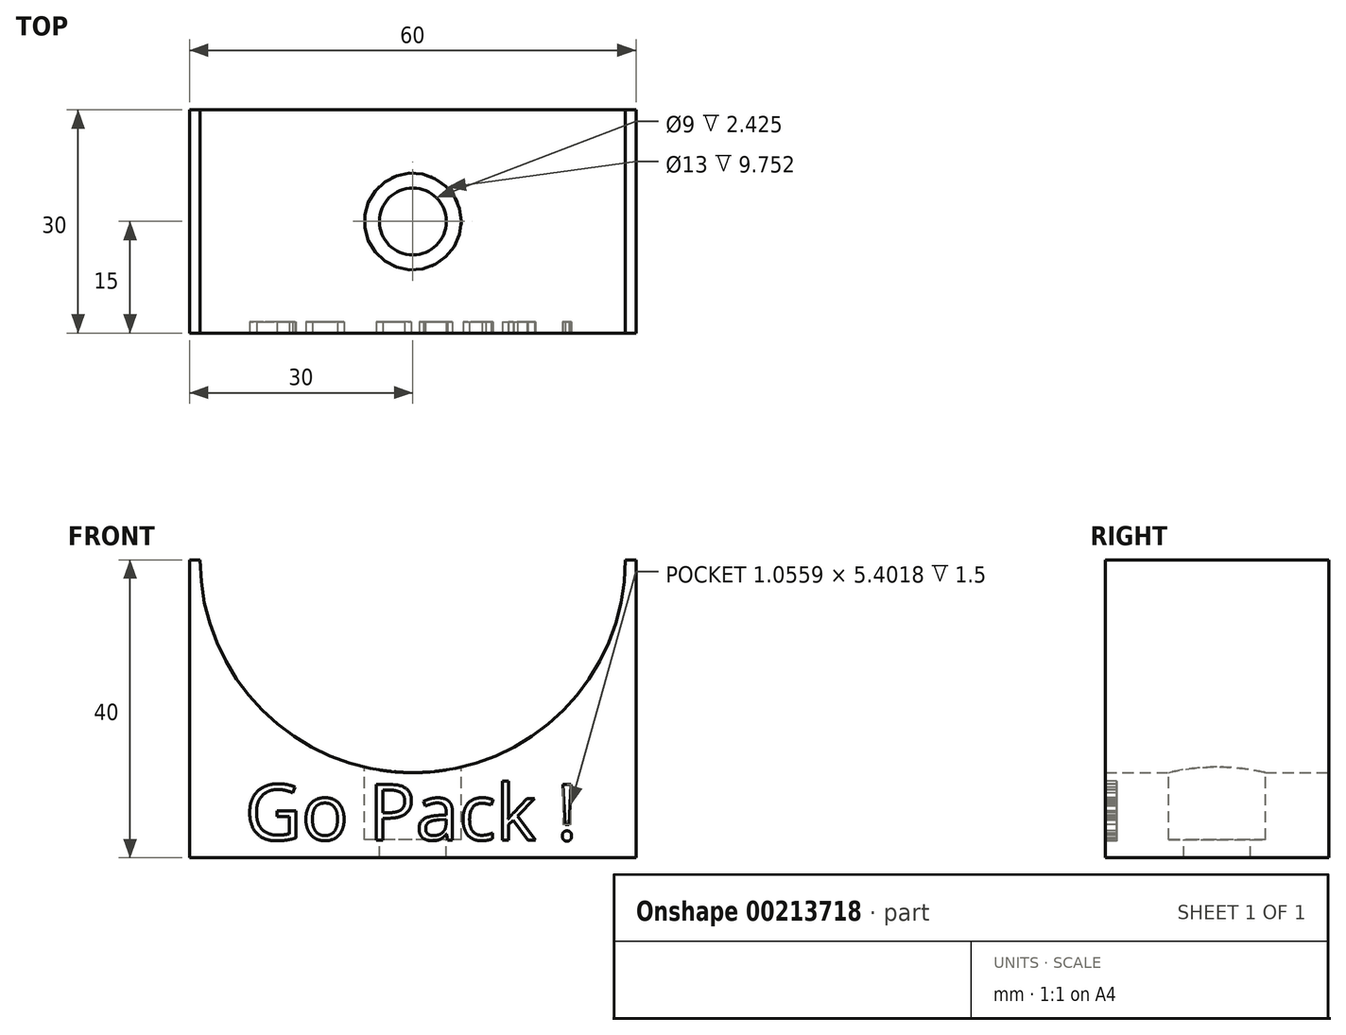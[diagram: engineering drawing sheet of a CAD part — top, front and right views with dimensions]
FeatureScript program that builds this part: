
annotation { "Feature Type Name" : "Feature", "Feature Type Description" : "" }
export const myFeature = defineFeature(function(context is Context, id is Id, definition is map)
    precondition{}
    {
        {
            var Q0;
            Q0=qCreatedBy(makeId("Front.planeOp"),FACE);
            var sketch = newSketch(context, id + "F0", { "sketchPlane" : qUnion([Q0])});
            skLineSegment(sketch, "E0.bottom", {"start": v(30, -20) * mm, "end": v(-30, -20) * mm});
            skLineSegment(sketch, "E0.top", {"start": v(30, 20) * mm, "end": v(-30, 20) * mm});
            skLineSegment(sketch, "E0.left", {"start": v(30, -20) * mm, "end": v(30, 20) * mm});
            skLineSegment(sketch, "E0.right", {"start": v(-30, -20) * mm, "end": v(-30, 20) * mm});
            skPoint(sketch, "E0.middle", {"position": v(0, 0) * mm});
            skLineSegment(sketch, "E1", {"start": v(0, 0) * mm, "end": v(0, 20) * mm});
            skPoint(sketch, "E2", {"position": v(0, 10) * mm});
            skCircle(sketch, "E3", {"center": v(0, 20) * mm, "radius": 28.57 * mm});
            skSolve(sketch);
        }
        {
            var Q0;
            Q0=makeQuery(id+"F0.imprint","IMPRINT",FACE,{"disambiguationData":[TD([[makeQuery(id+"F0.imprint","IMPRINT",EDGE,{"derivedFrom":sQuery(id+"F0.wireOp",EDGE,"E0.bottom")}),-1.0]])]});
            extrude(context, id + "F1", {"entities" : qUnion([Q0]), "depth" : 30 * mm});
        }
        {
            var Q0;
            Q0=qCreatedBy(makeId("Top.planeOp"),FACE);
            var sketch = newSketch(context, id + "F2", { "sketchPlane" : qUnion([Q0])});
            skLineSegment(sketch, "E4", {"start": v(0, 0) * mm, "end": v(0, -30) * mm});
            skPoint(sketch, "E5", {"position": v(0, -15) * mm});
            skSolve(sketch);
        }
        {
            var Q0;
            Q0=sQuery(id+"F2.wireOp",VERTEX,"E5");
            var Q1;
            Q1=makeQuery(id+"F1.opExtrude","SWEPT_BODY",BODY,{"disambiguationData":[OSD([sQuery(id+"F0.wireOp",EDGE,"E0.bottom"),sQuery(id+"F0.wireOp",EDGE,"E0.top"),sQuery(id+"F0.wireOp",EDGE,"E0.left"),sQuery(id+"F0.wireOp",EDGE,"E0.right"),sQuery(id+"F0.wireOp",EDGE,"E3")])]});
            hole(context, id + "F3", {"style" : HoleStyle.C_BORE, "endStyle" : HoleEndStyle.THROUGH, "holeDiameter" : 9 * mm, "cBoreDiameter" : 13 * mm, "cBoreDepth" : 9 * mm, "locations" : qUnion([Q0]), "scope" : qUnion([Q1]), "isTappedThrough" : true});
        }
        {
            var Q0;
            Q0=makeQuery(id+"F1.opExtrude","CAP_FACE",FACE,{"disambiguationData":[OSD([sQuery(id+"F0.wireOp",EDGE,"E0.bottom"),sQuery(id+"F0.wireOp",EDGE,"E0.top"),sQuery(id+"F0.wireOp",EDGE,"E0.left"),sQuery(id+"F0.wireOp",EDGE,"E0.right"),sQuery(id+"F0.wireOp",EDGE,"E3")])],"isStart":false});
            var sketch = newSketch(context, id + "F4", { "sketchPlane" : qUnion([Q0])});
            skText(sketch, "E6", { "text": "Go Pack !", "fontName": "OpenSans-Regular.ttf"});
            const initialGuessF4  = {"E6": [-0.02256, -0.01764, 1, 0, 0.00752]};
            skSetInitialGuess(sketch, initialGuessF4);
            skSolve(sketch);
        }
        {
            var Q0;
            Q0 = qSketchRegion(id + "F4", true);
            extrude(context, id + "F5", {"entities" : qUnion([Q0]), "operationType" : NewBodyOperationType.REMOVE, "oppositeDirection" : true, "depth" : 1.5 * mm});
        }
    });
